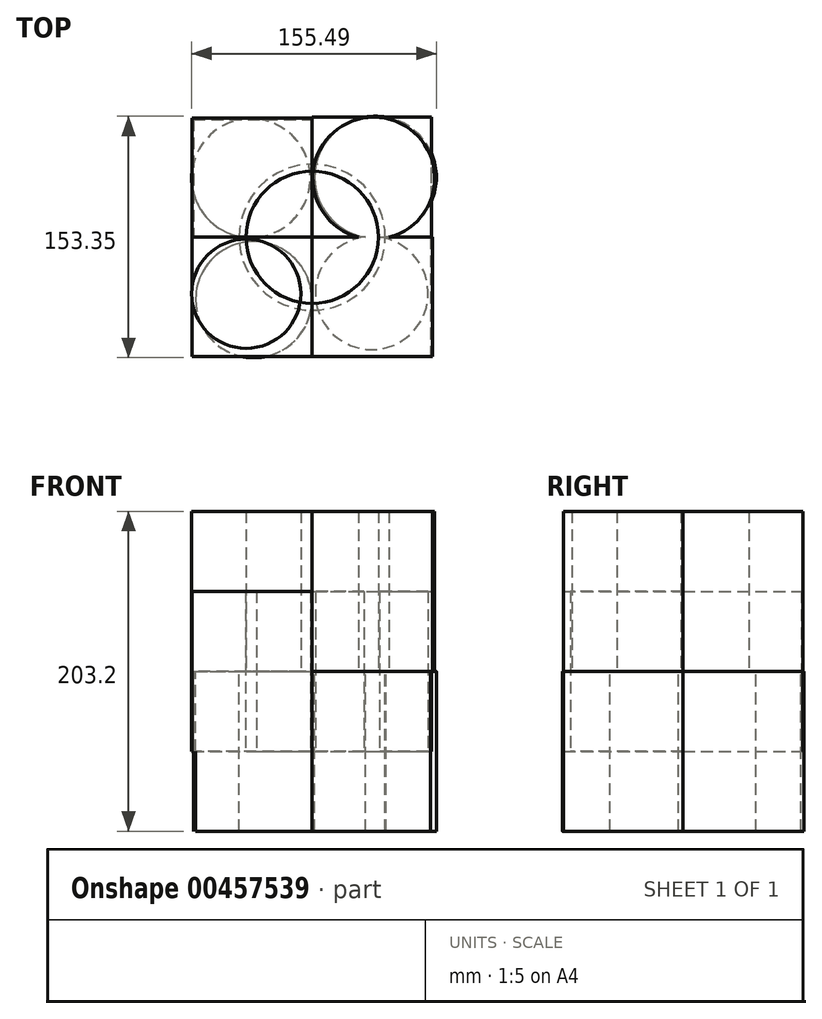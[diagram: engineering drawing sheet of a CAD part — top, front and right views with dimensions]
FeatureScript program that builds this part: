
annotation { "Feature Type Name" : "Feature", "Feature Type Description" : "" }
export const myFeature = defineFeature(function(context is Context, id is Id, definition is map)
    precondition{}
    {
        {
            var Q0;
            Q0=qCreatedBy(makeId("Top.planeOp"),FACE);
            var sketch = newSketch(context, id + "F0", { "sketchPlane" : qUnion([Q0])});
            skLineSegment(sketch, "E0.bottom", {"start": v(-76.24, -75.79) * mm, "end": v(0, -75.79) * mm});
            skLineSegment(sketch, "E0.top", {"start": v(-76.24, 0) * mm, "end": v(0, 0) * mm});
            skLineSegment(sketch, "E0.left", {"start": v(-76.24, -75.79) * mm, "end": v(-76.24, 0) * mm});
            skLineSegment(sketch, "E0.right", {"start": v(0, -75.79) * mm, "end": v(0, 0) * mm});
            skLineSegment(sketch, "E1.bottom", {"start": v(0, 0) * mm, "end": v(75.79, 0) * mm});
            skLineSegment(sketch, "E1.top", {"start": v(0, 76.24) * mm, "end": v(75.79, 76.24) * mm});
            skLineSegment(sketch, "E1.left", {"start": v(0, 0) * mm, "end": v(0, 76.24) * mm});
            skLineSegment(sketch, "E1.right", {"start": v(75.79, 0) * mm, "end": v(75.79, 76.24) * mm});
            skCircle(sketch, "E2", {"center": v(-38.88, 37.53) * mm, "radius": 37.7 * mm});
            skPoint(sketch, "E2.first.point", {"position": v(-65.54, 64.2) * mm});
            skPoint(sketch, "E2.second.point", {"position": v(-10.7, 12.48) * mm});
            skPoint(sketch, "E2.third.point", {"position": v(-4.01, 23.18) * mm});
            skCircle(sketch, "E3", {"center": v(37.83, -35.51) * mm, "radius": 35.84 * mm});
            skPoint(sketch, "E3.first.point", {"position": v(64.64, -59.3) * mm});
            skPoint(sketch, "E3.second.point", {"position": v(8.02, -15.6) * mm});
            skPoint(sketch, "E3.third.point", {"position": v(33, 0) * mm});
            skSolve(sketch);
        }
        {
            var Q0;
            Q0 = qSketchRegion(id + "F0", true);
            extrude(context, id + "F1", {"entities" : qUnion([Q0]), "endBound" : BoundingType.SYMMETRIC, "depth" : 101.6 * mm});
        }
        {
            var Q0;
            Q0=makeQuery(id+"F1.opExtrude","CAP_FACE",FACE,{"disambiguationData":[OSD([sQuery(id+"F0.wireOp",EDGE,"E1.bottom"),sQuery(id+"F0.wireOp",EDGE,"E1.top"),sQuery(id+"F0.wireOp",EDGE,"E1.left"),sQuery(id+"F0.wireOp",EDGE,"E1.right"),sQuery(id+"F0.wireOp",EDGE,"E3")])],"isStart":false});
            var sketch = newSketch(context, id + "F2", { "sketchPlane" : qUnion([Q0])});
            skCircle(sketch, "E4", {"center": v(0, 0) * mm, "radius": 41.98 * mm});
            skSolve(sketch);
        }
        {
            var Q0;
            Q0 = qSketchRegion(id + "F2", true);
            extrude(context, id + "F3", {"entities" : qUnion([Q0]), "endBound" : BoundingType.SYMMETRIC, "depth" : 101.6 * mm});
        }
        {
            var Q0;
            Q0=makeQuery(id+"F1.opExtrude","CAP_FACE",FACE,{"disambiguationData":[OSD([sQuery(id+"F0.wireOp",EDGE,"E0.bottom"),sQuery(id+"F0.wireOp",EDGE,"E0.top"),sQuery(id+"F0.wireOp",EDGE,"E0.left"),sQuery(id+"F0.wireOp",EDGE,"E0.right"),sQuery(id+"F0.wireOp",EDGE,"E2")])],"isStart":true});
            var sketch = newSketch(context, id + "F4", { "sketchPlane" : qUnion([Q0])});
            skCircle(sketch, "E5", {"center": v(0, 0) * mm, "radius": 46.37 * mm});
            skSolve(sketch);
        }
        {
            var Q0;
            Q0 = qSketchRegion(id + "F4", true);
            extrude(context, id + "F5", {"entities" : qUnion([Q0]), "endBound" : BoundingType.SYMMETRIC, "depth" : 101.6 * mm});
        }
        {
            var Q0;
            Q0=makeQuery(id+"F1.opExtrude","CAP_FACE",FACE,{"disambiguationData":[OSD([sQuery(id+"F0.wireOp",EDGE,"E0.bottom"),sQuery(id+"F0.wireOp",EDGE,"E0.top"),sQuery(id+"F0.wireOp",EDGE,"E0.left"),sQuery(id+"F0.wireOp",EDGE,"E0.right"),sQuery(id+"F0.wireOp",EDGE,"E2")])],"isStart":false});
            var sketch = newSketch(context, id + "F6", { "sketchPlane" : qUnion([Q0])});
            skLineSegment(sketch, "E6.bottom", {"start": v(-76.24, 0) * mm, "end": v(0, 0) * mm});
            skLineSegment(sketch, "E6.top", {"start": v(-76.24, 75.73) * mm, "end": v(0, 75.73) * mm});
            skLineSegment(sketch, "E6.left", {"start": v(-76.24, 0) * mm, "end": v(-76.24, 75.73) * mm});
            skLineSegment(sketch, "E6.right", {"start": v(0, 0) * mm, "end": v(0, 75.73) * mm});
            skLineSegment(sketch, "E7.bottom", {"start": v(76.38, 0) * mm, "end": v(0, 0) * mm});
            skLineSegment(sketch, "E7.top", {"start": v(76.38, -75.79) * mm, "end": v(0, -75.79) * mm});
            skLineSegment(sketch, "E7.left", {"start": v(76.38, 0) * mm, "end": v(76.38, -75.79) * mm});
            skLineSegment(sketch, "E7.right", {"start": v(0, 0) * mm, "end": v(0, -75.79) * mm});
            skCircle(sketch, "E8", {"center": v(-41.9, -35.9) * mm, "radius": 34.66 * mm});
            skPoint(sketch, "E8.first.point", {"position": v(-18.33, -61.3) * mm});
            skPoint(sketch, "E8.second.point", {"position": v(-64.67, -9.77) * mm});
            skPoint(sketch, "E8.third.point", {"position": v(-51.43, -2.57) * mm});
            skCircle(sketch, "E9", {"center": v(39.1, 37.52) * mm, "radius": 38.73 * mm});
            skPoint(sketch, "E9.first.point", {"position": v(62.85, 6.93) * mm});
            skPoint(sketch, "E9.second.point", {"position": v(14.78, 67.67) * mm});
            skPoint(sketch, "E9.third.point", {"position": v(24.57, 73.43) * mm});
            skSolve(sketch);
        }
        {
            var Q0;
            Q0 = qSketchRegion(id + "F6", true);
            extrude(context, id + "F7", {"entities" : qUnion([Q0]), "endBound" : BoundingType.SYMMETRIC, "depth" : 101.6 * mm});
        }
        {
            var Q0;
            Q0=makeQuery(id+"F1.opExtrude","CAP_FACE",FACE,{"disambiguationData":[OSD([sQuery(id+"F0.wireOp",EDGE,"E0.bottom"),sQuery(id+"F0.wireOp",EDGE,"E0.top"),sQuery(id+"F0.wireOp",EDGE,"E0.left"),sQuery(id+"F0.wireOp",EDGE,"E0.right"),sQuery(id+"F0.wireOp",EDGE,"E2")])],"isStart":true});
            var sketch = newSketch(context, id + "F8", { "sketchPlane" : qUnion([Q0])});
            skLineSegment(sketch, "E10.bottom", {"start": v(-75.38, -74.86) * mm, "end": v(0, -74.86) * mm});
            skLineSegment(sketch, "E10.top", {"start": v(-75.38, 0) * mm, "end": v(0, 0) * mm});
            skLineSegment(sketch, "E10.left", {"start": v(-75.38, -74.86) * mm, "end": v(-75.38, 0) * mm});
            skLineSegment(sketch, "E10.right", {"start": v(0, -74.86) * mm, "end": v(0, 0) * mm});
            skLineSegment(sketch, "E11.bottom", {"start": v(75.18, 0) * mm, "end": v(0, 0) * mm});
            skLineSegment(sketch, "E11.top", {"start": v(75.18, 75.79) * mm, "end": v(0, 75.79) * mm});
            skLineSegment(sketch, "E11.left", {"start": v(75.18, 0) * mm, "end": v(75.18, 75.79) * mm});
            skLineSegment(sketch, "E11.right", {"start": v(0, 0) * mm, "end": v(0, 75.79) * mm});
            skCircle(sketch, "E12", {"center": v(-37.12, 39.63) * mm, "radius": 36.92 * mm});
            skPoint(sketch, "E12.first.point", {"position": v(-14.64, 10.35) * mm});
            skPoint(sketch, "E12.second.point", {"position": v(-64.44, 64.47) * mm});
            skPoint(sketch, "E12.third.point", {"position": v(-44.58, 75.79) * mm});
            skCircle(sketch, "E13", {"center": v(40.24, -38.12) * mm, "radius": 38.68 * mm});
            skPoint(sketch, "E13.first.point", {"position": v(67.4, -65.65) * mm});
            skPoint(sketch, "E13.second.point", {"position": v(12.7, -10.96) * mm});
            skPoint(sketch, "E13.third.point", {"position": v(33.72, 0) * mm});
            skSolve(sketch);
        }
        {
            var Q0;
            Q0 = qSketchRegion(id + "F8", true);
            extrude(context, id + "F9", {"entities" : qUnion([Q0]), "endBound" : BoundingType.SYMMETRIC, "depth" : 101.6 * mm});
        }
    });
